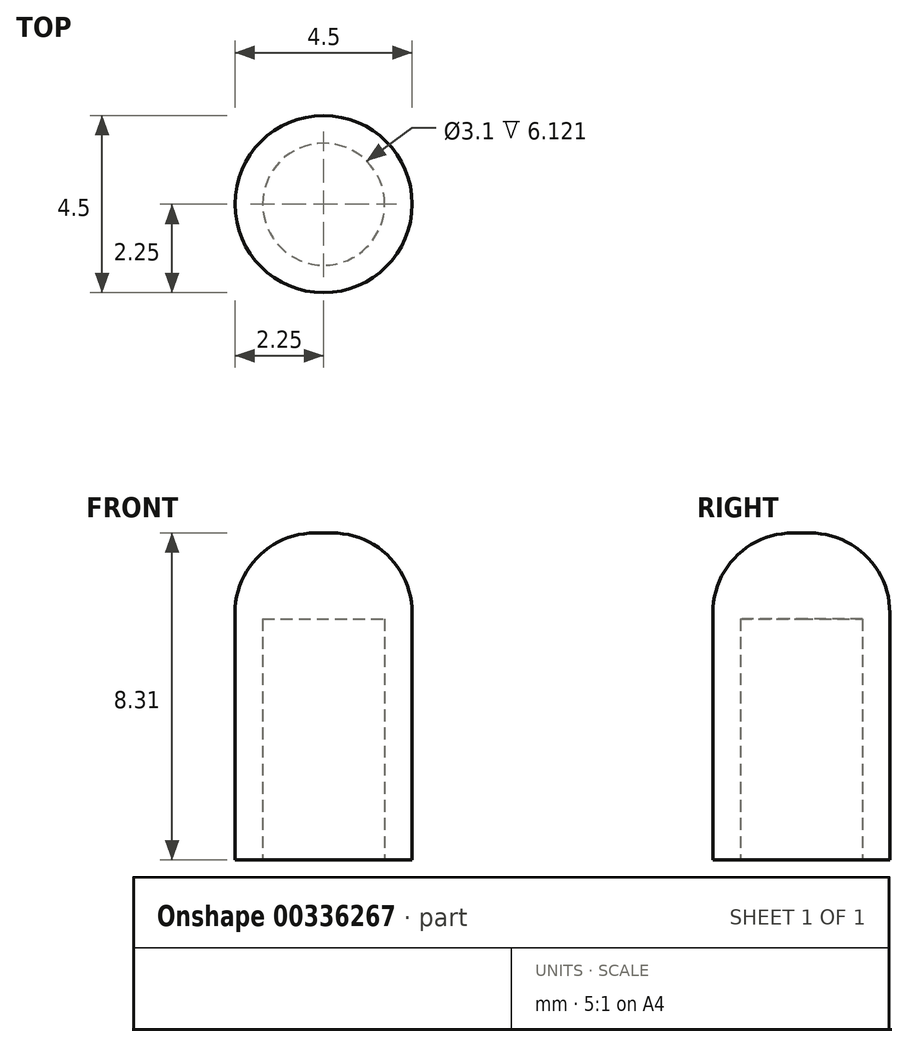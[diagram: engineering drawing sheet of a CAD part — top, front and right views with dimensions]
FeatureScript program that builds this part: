
annotation { "Feature Type Name" : "Feature", "Feature Type Description" : "" }
export const myFeature = defineFeature(function(context is Context, id is Id, definition is map)
    precondition{}
    {
        {
            var Q0;
            Q0=qCreatedBy(makeId("Top.planeOp"),FACE);
            var sketch = newSketch(context, id + "F0", { "sketchPlane" : qUnion([Q0])});
            skCircle(sketch, "E0", {"center": v(0, 0) * mm, "radius": 2.25 * mm});
            skSolve(sketch);
        }
        {
            var Q0;
            Q0=makeQuery(id+"F0.imprint","IMPRINT",FACE,{"disambiguationData":[TD([[makeQuery(id+"F0.imprint","IMPRINT",EDGE,{"derivedFrom":sQuery(id+"F0.wireOp",EDGE,"E0")}),1.0]])]});
            var Q1;
            Q1 = qConstructionFilter(qBodyType(qCreatedBy(id + "F0" ,EDGE), BodyType.WIRE), ConstructionObject.NO);
            extrude(context, id + "F1", {"entities" : qUnion([Q0]), "surfaceEntities" : qUnion([Q1]), "depth" : 8.3 * mm});
        }
        {
            var Q0;
            Q0=makeQuery(id+"F1.opExtrude","CAP_EDGE",EDGE,{"disambiguationData":[OSD([sQuery(id+"F0.wireOp",EDGE,"E0")])],"isStart":false});
            var Q1;
            Q1=makeQuery(id+"F1.opExtrude","CAP_FACE",FACE,{"disambiguationData":[OSD([sQuery(id+"F0.wireOp",EDGE,"E0")])],"isStart":false});
            fillet(context, id + "F2", {"entities" : qUnion([Q0, Q1]), "radius" : 2.03 * mm, "tangentPropagation" : true, "allowEdgeOverflow" : false});
        }
        {
            var Q0;
            Q0=makeQuery(id+"F1.opExtrude","CAP_FACE",FACE,{"disambiguationData":[OSD([sQuery(id+"F0.wireOp",EDGE,"E0")])],"isStart":true});
            var sketch = newSketch(context, id + "F3", { "sketchPlane" : qUnion([Q0])});
            skCircle(sketch, "E1", {"center": v(0, 0) * mm, "radius": 1.55 * mm});
            skSolve(sketch);
        }
        {
            var Q0;
            Q0=makeQuery(id+"F3.imprint","IMPRINT",FACE,{"disambiguationData":[TD([[makeQuery(id+"F3.imprint","IMPRINT",EDGE,{"derivedFrom":sQuery(id+"F3.wireOp",EDGE,"E1")}),1.0]])]});
            extrude(context, id + "F4", {"entities" : qUnion([Q0]), "operationType" : NewBodyOperationType.REMOVE, "oppositeDirection" : true, "depth" : 6.12 * mm});
        }
    });
